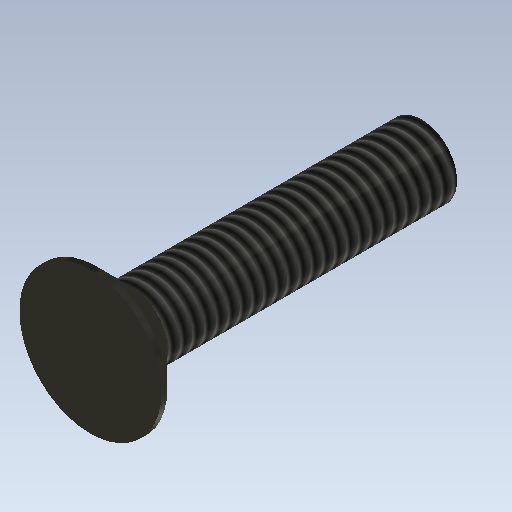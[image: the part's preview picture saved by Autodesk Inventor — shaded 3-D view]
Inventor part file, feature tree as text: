
AUTODESK INVENTOR PART (.ipt)
format: ipt  version: 2020.2 (Build 242310000, 310)  size: 168,960 bytes
history: native  units: mm
features: extrude x5, sketch x5, other x1, thread x1, chamfer x1
ambient origin geometry x1: Origin
bodies: Body1 (feature_tree)
feature tree (13):
  other  "ソリッド1"
  extrude  "押し出し1"  Depth=3.0mm
  extrude  "押し出し2"  Depth=6.0mm TaperAngle=0.0deg
  thread  "ねじ1"
  chamfer  "面取り1"  Distance=6.0mm
  extrude  "押し出し4"  Depth=1.75mm TaperAngle=0.0deg
  extrude  "押し出し5"  Depth=10.0mm TaperAngle=0.0deg
  extrude  "押し出し6"  Depth=1.5mm TaperAngle=45.0deg
  sketch  "スケッチ1"
  sketch  "スケッチ2"
  sketch  "スケッチ4"
  sketch  "スケッチ5"
  sketch  "スケッチ6"
